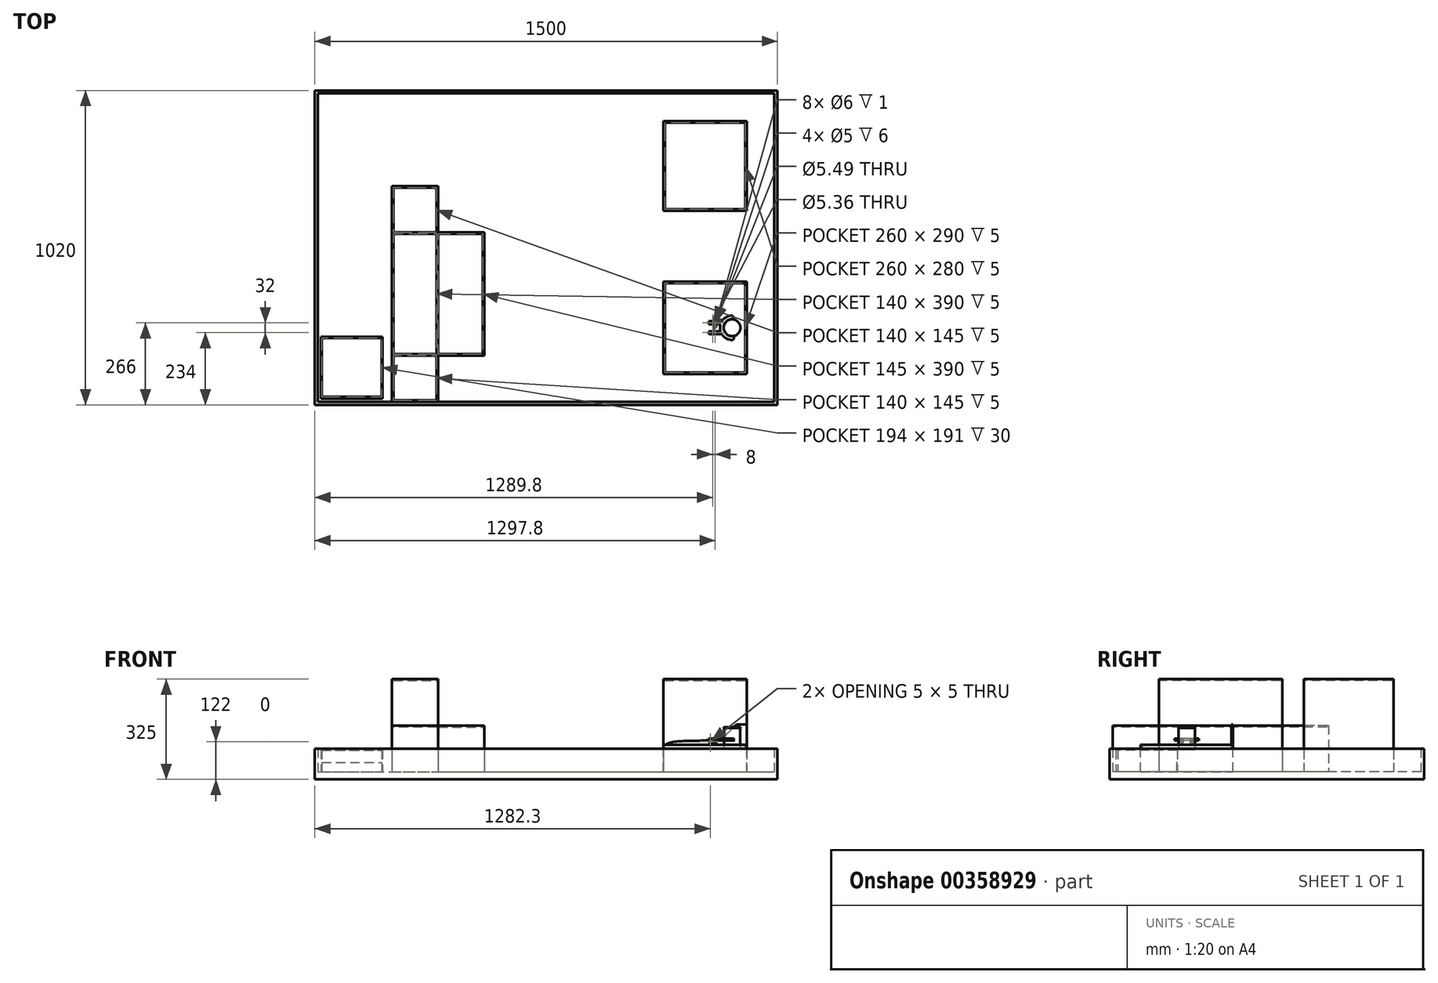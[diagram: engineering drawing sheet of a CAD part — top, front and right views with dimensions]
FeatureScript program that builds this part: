
annotation { "Feature Type Name" : "Feature", "Feature Type Description" : "" }
export const myFeature = defineFeature(function(context is Context, id is Id, definition is map)
    precondition{}
    {
        {
            var Q0;
            Q0=qCreatedBy(makeId("Top.planeOp"),FACE);
            var sketch = newSketch(context, id + "F0", { "sketchPlane" : qUnion([Q0])});
            skCircle(sketch, "E0", {"center": v(0, 0) * mm, "radius": 27.2 * mm});
            skSolve(sketch);
        }
        {
            var Q0;
            Q0=qSketchRegion(id+"F0",true);
            extrude(context, id + "F1", {"entities" : qUnion([Q0]), "depth" : 2.83 * mm});
        }
        {
            var Q0;
            Q0=makeQuery(id+"F1.opExtrude","CAP_FACE",FACE,{"disambiguationData":[OSD([sQuery(id+"F0.wireOp",EDGE,"E0")])],"isStart":false});
            var sketch = newSketch(context, id + "F2", { "sketchPlane" : qUnion([Q0])});
            skCircle(sketch, "E1", {"center": v(0, 0) * mm, "radius": 26.4 * mm});
            skSolve(sketch);
        }
        {
            var Q0;
            Q0=qSketchRegion(id+"F2",true);
            extrude(context, id + "F3", {"entities" : qUnion([Q0]), "operationType" : NewBodyOperationType.ADD, "depth" : 67.36 * mm});
        }
        {
            var Q0;
            Q0=makeQuery(id+"F3.opExtrude","CAP_FACE",FACE,{"disambiguationData":[OSD([sQuery(id+"F2.wireOp",EDGE,"E1")])],"isStart":false});
            var sketch = newSketch(context, id + "F4", { "sketchPlane" : qUnion([Q0])});
            skCircle(sketch, "E2", {"center": v(0, 0) * mm, "radius": 27.2 * mm});
            skSolve(sketch);
        }
        {
            var Q0;
            Q0=qSketchRegion(id+"F4",true);
            extrude(context, id + "F5", {"entities" : qUnion([Q0]), "operationType" : NewBodyOperationType.ADD, "depth" : 2.83 * mm});
        }
        {
            var Q0;
            Q0=makeQuery(id+"F5.opExtrude","CAP_FACE",FACE,{"disambiguationData":[OSD([sQuery(id+"F4.wireOp",EDGE,"E2")])],"isStart":false});
            var sketch = newSketch(context, id + "F6", { "sketchPlane" : qUnion([Q0])});
            skSolve(sketch);
        }
        {
            var Q0;
            Q0=qCreatedBy(makeId("Top.planeOp"),FACE);
            cPlane(context, id + "F7", {"entities" : qUnion([Q0]), "cplaneType" : CPlaneType.OFFSET, "offset" : 25 * mm, "width" : 150 * mm, "height" : 150 * mm});
        }
        {
            var Q0;
            Q0=makeQuery(id+"F6.imprint","IMPRINT",FACE,{"disambiguationData":[TD([[makeQuery(id+"F6.imprint","IMPRINT",EDGE,{"derivedFrom":makeQuery(id+"F5.opExtrude","CAP_EDGE",EDGE,{"disambiguationData":[OSD([sQuery(id+"F4.wireOp",EDGE,"E2")])],"isStart":false})}),1.0]])]});
            var sketch = newSketch(context, id + "F8", { "sketchPlane" : qUnion([Q0])});
            skSolve(sketch);
        }
        {
            var Q0;
            Q0=qCreatedBy(makeId("Top.planeOp"),FACE);
            var sketch = newSketch(context, id + "F9", { "sketchPlane" : qUnion([Q0])});
            skLineSegment(sketch, "E3.bottom", {"start": v(-222.8, -150) * mm, "end": v(47.2, -150) * mm});
            skLineSegment(sketch, "E3.top", {"start": v(-222.8, 150) * mm, "end": v(47.2, 150) * mm});
            skLineSegment(sketch, "E3.left", {"start": v(-222.8, -150) * mm, "end": v(-222.8, 150) * mm});
            skLineSegment(sketch, "E3.right", {"start": v(47.2, -150) * mm, "end": v(47.2, 150) * mm});
            skSolve(sketch);
        }
        {
            var Q0;
            Q0=qSketchRegion(id+"F9",true);
            extrude(context, id + "F10", {"entities" : qUnion([Q0]), "oppositeDirection" : true, "depth" : 72 * mm});
        }
        {
            var Q0;
            Q0=makeQuery(id+"F10.opExtrude","CAP_FACE",FACE,{"disambiguationData":[OSD([sQuery(id+"F9.wireOp",EDGE,"E3.bottom"),sQuery(id+"F9.wireOp",EDGE,"E3.top"),sQuery(id+"F9.wireOp",EDGE,"E3.left"),sQuery(id+"F9.wireOp",EDGE,"E3.right")])],"isStart":true});
            var sketch = newSketch(context, id + "F11", { "sketchPlane" : qUnion([Q0])});
            skLineSegment(sketch, "E4.bottom", {"start": v(-222.8, -150) * mm, "end": v(47.2, -150) * mm});
            skLineSegment(sketch, "E4.top", {"start": v(-222.8, -145) * mm, "end": v(42.2, -145) * mm});
            skLineSegment(sketch, "E4.left", {"start": v(-222.8, -150) * mm, "end": v(-222.8, -145) * mm});
            skLineSegment(sketch, "E5.bottom", {"start": v(47.2, 150) * mm, "end": v(42.2, 150) * mm});
            skLineSegment(sketch, "E5.left", {"start": v(47.2, 150) * mm, "end": v(47.2, -150) * mm});
            skLineSegment(sketch, "E5.right", {"start": v(42.2, 150) * mm, "end": v(42.2, -145) * mm});
            skSolve(sketch);
        }
        {
            var Q0;
            Q0=qSketchRegion(id+"F11",true);
            extrude(context, id + "F12", {"entities" : qUnion([Q0]), "operationType" : NewBodyOperationType.ADD, "depth" : 15 * mm});
        }
        {
            var Q0;
            Q0=makeQuery(id+"F12.boolean.opBoolean","MERGE",FACE,{"derivedFrom":[makeQuery(id+"F10.opExtrude","SWEPT_FACE",FACE,{"disambiguationData":[OSD([sQuery(id+"F9.wireOp",EDGE,"E3.top")])]}),makeQuery(id+"F12.opExtrude","SWEPT_FACE",FACE,{"disambiguationData":[OSD([sQuery(id+"F11.wireOp",EDGE,"E5.bottom")])]})]});
            var sketch = newSketch(context, id + "F13", { "sketchPlane" : qUnion([Q0])});
            skLineSegment(sketch, "E6", {"start": v(-47.2, 81.36) * mm, "end": v(-21.31, 81.36) * mm});
            skFitSpline(sketch, "E7", {"points": [v(-21.31, 81.36) * mm, v(15.24, 52.01) * mm, v(114.14, 28.17) * mm, v(222.8, 0) * mm], "startDerivative": vector(181.02, 0.3) * mm, "endDerivative": vector(-1.73, -239.85) * mm});
            skLineSegment(sketch, "E8", {"start": v(-47.2, 81.36) * mm, "end": v(-47.2, -72) * mm});
            skLineSegment(sketch, "E9", {"start": v(-47.2, -72) * mm, "end": v(222.8, -72) * mm});
            skLineSegment(sketch, "E10", {"start": v(222.8, -72) * mm, "end": v(222.8, 0) * mm});
            skSolve(sketch);
        }
        {
            var Q0;
            Q0=qSketchRegion(id+"F13",true);
            extrude(context, id + "F14", {"entities" : qUnion([Q0]), "operationType" : NewBodyOperationType.ADD, "oppositeDirection" : true, "depth" : 5 * mm});
        }
        {
            var Q0;
            Q0=makeQuery(id+"F10.opExtrude","CAP_FACE",FACE,{"disambiguationData":[OSD([sQuery(id+"F9.wireOp",EDGE,"E3.bottom"),sQuery(id+"F9.wireOp",EDGE,"E3.top"),sQuery(id+"F9.wireOp",EDGE,"E3.left"),sQuery(id+"F9.wireOp",EDGE,"E3.right")])],"isStart":true});
            var sketch = newSketch(context, id + "F15", { "sketchPlane" : qUnion([Q0])});
            skLineSegment(sketch, "E11.bottom", {"start": v(-222.8, 145) * mm, "end": v(-217.8, 145) * mm});
            skLineSegment(sketch, "E11.top", {"start": v(-222.8, -145) * mm, "end": v(-217.8, -145) * mm});
            skLineSegment(sketch, "E11.left", {"start": v(-222.8, 145) * mm, "end": v(-222.8, -145) * mm});
            skLineSegment(sketch, "E11.right", {"start": v(-217.8, 145) * mm, "end": v(-217.8, -145) * mm});
            skSolve(sketch);
        }
        {
            var Q0;
            Q0=qSketchRegion(id+"F15",true);
            extrude(context, id + "F16", {"entities" : qUnion([Q0]), "operationType" : NewBodyOperationType.ADD, "depth" : 5 * mm});
        }
        {
            var Q0;
            Q0=makeQuery(id+"F10.opExtrude","CAP_FACE",FACE,{"disambiguationData":[OSD([sQuery(id+"F9.wireOp",EDGE,"E3.bottom"),sQuery(id+"F9.wireOp",EDGE,"E3.top"),sQuery(id+"F9.wireOp",EDGE,"E3.left"),sQuery(id+"F9.wireOp",EDGE,"E3.right")])],"isStart":false});
            var sketch = newSketch(context, id + "F17", { "sketchPlane" : qUnion([Q0])});
            skLineSegment(sketch, "E12.bottom", {"start": v(147.2, 250) * mm, "end": v(-1352.8, 250) * mm});
            skLineSegment(sketch, "E12.top", {"start": v(147.2, -770) * mm, "end": v(-1352.8, -770) * mm});
            skLineSegment(sketch, "E12.left", {"start": v(147.2, 250) * mm, "end": v(147.2, -770) * mm});
            skLineSegment(sketch, "E12.right", {"start": v(-1352.8, 250) * mm, "end": v(-1352.8, -770) * mm});
            skSolve(sketch);
        }
        {
            var Q0;
            Q0=qSketchRegion(id+"F17",true);
            extrude(context, id + "F18", {"entities" : qUnion([Q0]), "operationType" : NewBodyOperationType.ADD, "depth" : 25 * mm});
        }
        {
            var Q0;
            Q0=makeQuery(id+"F18.opExtrude","CAP_FACE",FACE,{"disambiguationData":[OSD([sQuery(id+"F17.wireOp",EDGE,"E12.bottom"),sQuery(id+"F17.wireOp",EDGE,"E12.top"),sQuery(id+"F17.wireOp",EDGE,"E12.left"),sQuery(id+"F17.wireOp",EDGE,"E12.right")])],"isStart":true});
            var sketch = newSketch(context, id + "F19", { "sketchPlane" : qUnion([Q0])});
            skLineSegment(sketch, "E13.bottom", {"start": v(-222.8, 670) * mm, "end": v(47.2, 670) * mm});
            skLineSegment(sketch, "E13.top", {"start": v(-222.8, 380) * mm, "end": v(47.2, 380) * mm});
            skLineSegment(sketch, "E13.left", {"start": v(-222.8, 670) * mm, "end": v(-222.8, 380) * mm});
            skLineSegment(sketch, "E13.right", {"start": v(47.2, 670) * mm, "end": v(47.2, 380) * mm});
            skSolve(sketch);
        }
        {
            var Q0;
            Q0=qSketchRegion(id+"F19",true);
            extrude(context, id + "F20", {"entities" : qUnion([Q0]), "operationType" : NewBodyOperationType.ADD, "depth" : 300 * mm});
        }
        {
            var Q0;
            Q0=makeQuery(id+"F20.opExtrude","CAP_FACE",FACE,{"disambiguationData":[OSD([sQuery(id+"F19.wireOp",EDGE,"E13.bottom"),sQuery(id+"F19.wireOp",EDGE,"E13.top"),sQuery(id+"F19.wireOp",EDGE,"E13.left"),sQuery(id+"F19.wireOp",EDGE,"E13.right")])],"isStart":false});
            var sketch = newSketch(context, id + "F21", { "sketchPlane" : qUnion([Q0])});
            skLineSegment(sketch, "E14.bottom", {"start": v(-217.8, 665) * mm, "end": v(42.2, 665) * mm});
            skLineSegment(sketch, "E14.top", {"start": v(-217.8, 385) * mm, "end": v(42.2, 385) * mm});
            skLineSegment(sketch, "E14.left", {"start": v(-217.8, 665) * mm, "end": v(-217.8, 385) * mm});
            skLineSegment(sketch, "E14.right", {"start": v(42.2, 665) * mm, "end": v(42.2, 385) * mm});
            skSolve(sketch);
        }
        {
            var Q0;
            Q0=qSketchRegion(id+"F21",true);
            extrude(context, id + "F22", {"entities" : qUnion([Q0]), "operationType" : NewBodyOperationType.REMOVE, "oppositeDirection" : true, "depth" : 5 * mm});
        }
        {
            var Q0;
            Q0=makeQuery(id+"F18.opExtrude","CAP_FACE",FACE,{"disambiguationData":[OSD([sQuery(id+"F17.wireOp",EDGE,"E12.bottom"),sQuery(id+"F17.wireOp",EDGE,"E12.top"),sQuery(id+"F17.wireOp",EDGE,"E12.left"),sQuery(id+"F17.wireOp",EDGE,"E12.right")])],"isStart":true});
            var sketch = newSketch(context, id + "F23", { "sketchPlane" : qUnion([Q0])});
            skLineSegment(sketch, "E15.bottom", {"start": v(-1352.8, 770) * mm, "end": v(147.2, 770) * mm});
            skLineSegment(sketch, "E15.top", {"start": v(-1352.8, -250) * mm, "end": v(147.2, -250) * mm});
            skLineSegment(sketch, "E15.left", {"start": v(-1352.8, 770) * mm, "end": v(-1352.8, -250) * mm});
            skLineSegment(sketch, "E15.right", {"start": v(147.2, 770) * mm, "end": v(147.2, -250) * mm});
            skLineSegment(sketch, "E16.bottom", {"start": v(-1342.8, 760) * mm, "end": v(137.2, 760) * mm});
            skLineSegment(sketch, "E16.top", {"start": v(-1342.8, -240) * mm, "end": v(137.2, -240) * mm});
            skLineSegment(sketch, "E16.left", {"start": v(-1342.8, 760) * mm, "end": v(-1342.8, -240) * mm});
            skLineSegment(sketch, "E16.right", {"start": v(137.2, 760) * mm, "end": v(137.2, -240) * mm});
            skSolve(sketch);
        }
        {
            var Q0;
            Q0=qSketchRegion(id+"F23",true);
            extrude(context, id + "F24", {"entities" : qUnion([Q0]), "operationType" : NewBodyOperationType.ADD, "depth" : 75 * mm});
        }
        {
            var Q0;
            Q0=makeQuery(id+"F18.opExtrude","CAP_FACE",FACE,{"disambiguationData":[OSD([sQuery(id+"F17.wireOp",EDGE,"E12.bottom"),sQuery(id+"F17.wireOp",EDGE,"E12.top"),sQuery(id+"F17.wireOp",EDGE,"E12.left"),sQuery(id+"F17.wireOp",EDGE,"E12.right")])],"isStart":true});
            var sketch = newSketch(context, id + "F25", { "sketchPlane" : qUnion([Q0])});
            skLineSegment(sketch, "E17.bottom", {"start": v(-1102.8, 460) * mm, "end": v(-952.8, 460) * mm});
            skLineSegment(sketch, "E17.top", {"start": v(-1102.8, -240) * mm, "end": v(-952.8, -240) * mm});
            skLineSegment(sketch, "E17.left", {"start": v(-1102.8, 460) * mm, "end": v(-1102.8, -240) * mm});
            skLineSegment(sketch, "E17.right", {"start": v(-952.8, 460) * mm, "end": v(-952.8, 310) * mm});
            skLineSegment(sketch, "E18.bottom", {"start": v(-952.8, 310) * mm, "end": v(-802.8, 310) * mm});
            skLineSegment(sketch, "E18.top", {"start": v(-952.8, -90) * mm, "end": v(-802.8, -90) * mm});
            skLineSegment(sketch, "E18.right", {"start": v(-802.8, 310) * mm, "end": v(-802.8, -90) * mm});
            skLineSegment(sketch, "E19.trimOffspring", {"start": v(-952.8, -90) * mm, "end": v(-952.8, -240) * mm});
            skSolve(sketch);
        }
        {
            var Q0;
            Q0=qSketchRegion(id+"F25",true);
            extrude(context, id + "F26", {"entities" : qUnion([Q0]), "operationType" : NewBodyOperationType.ADD, "depth" : 150 * mm});
        }
        {
            var Q0;
            Q0=makeQuery(id+"F26.opExtrude","CAP_FACE",FACE,{"disambiguationData":[OSD([sQuery(id+"F25.wireOp",EDGE,"E17.bottom"),sQuery(id+"F25.wireOp",EDGE,"E17.top"),sQuery(id+"F25.wireOp",EDGE,"E17.left"),sQuery(id+"F25.wireOp",EDGE,"E17.right"),sQuery(id+"F25.wireOp",EDGE,"E18.bottom"),sQuery(id+"F25.wireOp",EDGE,"E18.top"),sQuery(id+"F25.wireOp",EDGE,"E18.right"),sQuery(id+"F25.wireOp",EDGE,"E19.trimOffspring")])],"isStart":false});
            var sketch = newSketch(context, id + "F27", { "sketchPlane" : qUnion([Q0])});
            skLineSegment(sketch, "E20.bottom", {"start": v(-952.8, 310) * mm, "end": v(-1102.8, 310) * mm});
            skLineSegment(sketch, "E20.top", {"start": v(-952.8, -90) * mm, "end": v(-1102.8, -90) * mm});
            skLineSegment(sketch, "E20.left", {"start": v(-952.8, 310) * mm, "end": v(-952.8, -90) * mm});
            skLineSegment(sketch, "E20.right", {"start": v(-1102.8, 310) * mm, "end": v(-1102.8, -90) * mm});
            skSolve(sketch);
        }
        {
            var Q0;
            Q0=qSketchRegion(id+"F27",true);
            extrude(context, id + "F28", {"entities" : qUnion([Q0]), "operationType" : NewBodyOperationType.ADD, "depth" : 150 * mm});
        }
        {
            var Q0;
            Q0=makeQuery(id+"F28.opExtrude","CAP_FACE",FACE,{"disambiguationData":[OSD([sQuery(id+"F27.wireOp",EDGE,"E20.bottom"),sQuery(id+"F27.wireOp",EDGE,"E20.top"),sQuery(id+"F27.wireOp",EDGE,"E20.left"),sQuery(id+"F27.wireOp",EDGE,"E20.right")])],"isStart":false});
            var sketch = newSketch(context, id + "F29", { "sketchPlane" : qUnion([Q0])});
            skLineSegment(sketch, "E21.bottom", {"start": v(-1097.8, 305) * mm, "end": v(-957.8, 305) * mm});
            skLineSegment(sketch, "E21.top", {"start": v(-1097.8, -85) * mm, "end": v(-957.8, -85) * mm});
            skLineSegment(sketch, "E21.left", {"start": v(-1097.8, 305) * mm, "end": v(-1097.8, -85) * mm});
            skLineSegment(sketch, "E21.right", {"start": v(-957.8, 305) * mm, "end": v(-957.8, -85) * mm});
            skSolve(sketch);
        }
        {
            var Q0;
            Q0=qSketchRegion(id+"F29",true);
            extrude(context, id + "F30", {"entities" : qUnion([Q0]), "operationType" : NewBodyOperationType.REMOVE, "oppositeDirection" : true, "depth" : 5 * mm});
        }
        {
            var Q0;
            {var subQ0=sQuery(id+"F25.wireOp",EDGE,"E17.left");var subQ1=sQuery(id+"F25.wireOp",EDGE,"E18.bottom");var subQ2=sQuery(id+"F25.wireOp",EDGE,"E17.right");var subQ3=sQuery(id+"F25.wireOp",EDGE,"E17.bottom");var subQ4=makeQuery(id+"F26.opExtrude","CAP_FACE",FACE,{"disambiguationData":[OSD([subQ3,sQuery(id+"F25.wireOp",EDGE,"E17.top"),subQ0,subQ2,subQ1,sQuery(id+"F25.wireOp",EDGE,"E18.top"),sQuery(id+"F25.wireOp",EDGE,"E18.right"),sQuery(id+"F25.wireOp",EDGE,"E19.trimOffspring")])],"isStart":false});Q0=makeQuery(id+"F28.boolean.opBoolean","SPLIT",FACE,{"disambiguationData":[TD([makeQuery(id+"F26.opExtrude","SWEPT_FACE",FACE,{"disambiguationData":[OSD([subQ3])]})])],"derivedFrom":subQ4});}
            var sketch = newSketch(context, id + "F31", { "sketchPlane" : qUnion([Q0])});
            skLineSegment(sketch, "E22.bottom", {"start": v(-1097.8, 455) * mm, "end": v(-957.8, 455) * mm});
            skLineSegment(sketch, "E22.top", {"start": v(-1097.8, 310) * mm, "end": v(-957.8, 310) * mm});
            skLineSegment(sketch, "E22.left", {"start": v(-1097.8, 455) * mm, "end": v(-1097.8, 310) * mm});
            skLineSegment(sketch, "E22.right", {"start": v(-957.8, 455) * mm, "end": v(-957.8, 310) * mm});
            skLineSegment(sketch, "E23.bottom", {"start": v(-952.8, 305) * mm, "end": v(-807.8, 305) * mm});
            skLineSegment(sketch, "E23.top", {"start": v(-952.8, -85) * mm, "end": v(-807.8, -85) * mm});
            skLineSegment(sketch, "E23.left", {"start": v(-952.8, 305) * mm, "end": v(-952.8, -85) * mm});
            skLineSegment(sketch, "E23.right", {"start": v(-807.8, 305) * mm, "end": v(-807.8, -85) * mm});
            skLineSegment(sketch, "E24.bottom", {"start": v(-1097.8, -90) * mm, "end": v(-957.8, -90) * mm});
            skLineSegment(sketch, "E24.top", {"start": v(-1097.8, -235) * mm, "end": v(-957.8, -235) * mm});
            skLineSegment(sketch, "E24.left", {"start": v(-1097.8, -90) * mm, "end": v(-1097.8, -235) * mm});
            skLineSegment(sketch, "E24.right", {"start": v(-957.8, -90) * mm, "end": v(-957.8, -235) * mm});
            skSolve(sketch);
        }
        {
            var Q0;
            Q0=qSketchRegion(id+"F31",true);
            extrude(context, id + "F32", {"entities" : qUnion([Q0]), "operationType" : NewBodyOperationType.REMOVE, "oppositeDirection" : true, "depth" : 5 * mm});
        }
        {
            var Q0;
            Q0=qCreatedBy(id+"F7.planeOp",FACE);
            var sketch = newSketch(context, id + "F33", { "sketchPlane" : qUnion([Q0])});
            skLineSegment(sketch, "E25", {"start": v(0, 0) * mm, "end": v(-90, 0) * mm, "construction": true});
            skLineSegment(sketch, "E26.bottom", {"start": v(-74.5, -12) * mm, "end": v(-55, -12) * mm});
            skLineSegment(sketch, "E26.top", {"start": v(-74.5, -20) * mm, "end": v(-55, -20) * mm});
            skLineSegment(sketch, "E26.left", {"start": v(-74.5, -12) * mm, "end": v(-74.5, -13) * mm});
            skPoint(sketch, "E27.visualSharp", {"position": v(-51, -12) * mm});
            skPoint(sketch, "E28.visualSharp", {"position": v(-51, -20) * mm});
            skCircle(sketch, "E29", {"center": v(-55, -16) * mm, "radius": 3 * mm});
            skLineSegment(sketch, "E30", {"start": v(-59, -3.98) * mm, "end": v(-59, -18.08) * mm, "construction": true});
            skCircle(sketch, "E31.MirrorC", {"center": v(-63, -16) * mm, "radius": 3 * mm});
            skLineSegment(sketch, "E32.bottom", {"start": v(-74.5, -13) * mm, "end": v(-65.65, -13) * mm});
            skLineSegment(sketch, "E32.top", {"start": v(-74.5, -19) * mm, "end": v(-65.65, -19) * mm});
            skArc(sketch, "E33", {"start": v(-65.65, -13) * mm, "mid": v(-67, -16) * mm, "end": v(-65.65, -19) * mm});
            skLineSegment(sketch, "E34.trimOffspring", {"start": v(-74.5, -19) * mm, "end": v(-74.5, -20) * mm});
            skArc(sketch, "E35.trimOffspring", {"start": v(-55, -20) * mm, "mid": v(-51, -16) * mm, "end": v(-55, -12) * mm});
            skLineSegment(sketch, "E36.MirrorCS", {"start": v(-74.5, 12) * mm, "end": v(-74.5, 13) * mm});
            skLineSegment(sketch, "E37.MirrorCS", {"start": v(-74.5, 19) * mm, "end": v(-74.5, 20) * mm});
            skPoint(sketch, "E38.MirrorP", {"position": v(-51, 12) * mm});
            skLineSegment(sketch, "E39.MirrorCS", {"start": v(-74.5, 12) * mm, "end": v(-55, 12) * mm});
            skPoint(sketch, "E40.MirrorP", {"position": v(-51, 20) * mm});
            skArc(sketch, "E41.MirrorCS", {"start": v(-65.65, 13) * mm, "mid": v(-67, 16) * mm, "end": v(-65.65, 19) * mm});
            skArc(sketch, "E42.MirrorCS", {"start": v(-55, 20) * mm, "mid": v(-51, 16) * mm, "end": v(-55, 12) * mm});
            skLineSegment(sketch, "E43.MirrorCS", {"start": v(-74.5, 20) * mm, "end": v(-55, 20) * mm});
            skCircle(sketch, "E44.MirrorC", {"center": v(-55, 16) * mm, "radius": 3 * mm});
            skCircle(sketch, "E45.MirrorC", {"center": v(-63, 16) * mm, "radius": 3 * mm});
            skLineSegment(sketch, "E46.MirrorCS", {"start": v(-74.5, 19) * mm, "end": v(-65.65, 19) * mm});
            skLineSegment(sketch, "E47.MirrorCS", {"start": v(-74.5, 13) * mm, "end": v(-65.65, 13) * mm});
            skSolve(sketch);
        }
        {
            var Q0;
            Q0=qSketchRegion(id+"F33",true);
            var Q1;
            Q1=qSketchRegion(id+"F36",true);
            extrude(context, id + "F34", {"entities" : qUnion([Q0, Q1]), "endBound" : BoundingType.SYMMETRIC, "depth" : 8 * mm});
        }
        {
            var Q0;
            Q0=makeQuery(id+"F34.opExtrude","CAP_EDGE",EDGE,{"disambiguationData":[OSD([sQuery(id+"F33.wireOp",EDGE,"E34.trimOffspring")])],"isStart":false});
            var Q1;
            Q1=makeQuery(id+"F34.opExtrude","CAP_EDGE",EDGE,{"disambiguationData":[OSD([sQuery(id+"F33.wireOp",EDGE,"E26.left")])],"isStart":false});
            var Q2;
            Q2=makeQuery(id+"F34.opExtrude","CAP_EDGE",EDGE,{"disambiguationData":[OSD([sQuery(id+"F33.wireOp",EDGE,"E34.trimOffspring")])],"isStart":true});
            var Q3;
            Q3=makeQuery(id+"F34.opExtrude","CAP_EDGE",EDGE,{"disambiguationData":[OSD([sQuery(id+"F33.wireOp",EDGE,"E26.left")])],"isStart":true});
            var Q4;
            Q4=makeQuery(id+"F34.opExtrude","CAP_EDGE",EDGE,{"disambiguationData":[OSD([sQuery(id+"F33.wireOp",EDGE,"E36.MirrorCS")])],"isStart":false});
            var Q5;
            Q5=makeQuery(id+"F34.opExtrude","CAP_EDGE",EDGE,{"disambiguationData":[OSD([sQuery(id+"F33.wireOp",EDGE,"E37.MirrorCS")])],"isStart":false});
            var Q6;
            Q6=makeQuery(id+"F34.opExtrude","CAP_EDGE",EDGE,{"disambiguationData":[OSD([sQuery(id+"F33.wireOp",EDGE,"E37.MirrorCS")])],"isStart":true});
            var Q7;
            Q7=makeQuery(id+"F34.opExtrude","CAP_EDGE",EDGE,{"disambiguationData":[OSD([sQuery(id+"F33.wireOp",EDGE,"E36.MirrorCS")])],"isStart":true});
            fillet(context, id + "F35", {"entities" : qUnion([Q0, Q1, Q2, Q3, Q4, Q5, Q6, Q7]), "radius" : 4 * mm, "tangentPropagation" : true, "allowEdgeOverflow" : false});
        }
        {
            var Q0;
            Q0=makeQuery(id+"F34.opExtrude","SWEPT_FACE",FACE,{"disambiguationData":[OSD([sQuery(id+"F33.wireOp",EDGE,"E26.top")])]});
            var sketch = newSketch(context, id + "F36", { "sketchPlane" : qUnion([Q0])});
            skCircle(sketch, "E48", {"center": v(-70.5, 25) * mm, "radius": 3 * mm});
            skSolve(sketch);
        }
        {
            var Q0;
            Q0=qSketchRegion(id+"F36",true);
            var Q1;
            Q1=makeQuery(id+"F34.opExtrude","SWEPT_FACE",FACE,{"disambiguationData":[OSD([sQuery(id+"F33.wireOp",EDGE,"E26.bottom")])]});
            extrude(context, id + "F37", {"entities" : qUnion([Q0]), "operationType" : NewBodyOperationType.ADD, "endBound" : BoundingType.UP_TO_SURFACE, "oppositeDirection" : true, "endBoundEntityFace" : qUnion([Q1]), "depth" : 25 * mm});
        }
        {
            var Q0;
            Q0=makeQuery(id+"F34.opExtrude","SWEPT_FACE",FACE,{"disambiguationData":[OSD([sQuery(id+"F33.wireOp",EDGE,"E43.MirrorCS")])]});
            var sketch = newSketch(context, id + "F38", { "sketchPlane" : qUnion([Q0])});
            skCircle(sketch, "E49", {"center": v(70.5, 25) * mm, "radius": 3 * mm});
            skSolve(sketch);
        }
        {
            var Q0;
            Q0=qSketchRegion(id+"F38",true);
            var Q1;
            Q1=makeQuery(id+"F34.opExtrude","SWEPT_FACE",FACE,{"disambiguationData":[OSD([sQuery(id+"F33.wireOp",EDGE,"E39.MirrorCS")])]});
            extrude(context, id + "F39", {"entities" : qUnion([Q0]), "operationType" : NewBodyOperationType.ADD, "endBound" : BoundingType.UP_TO_SURFACE, "oppositeDirection" : true, "endBoundEntityFace" : qUnion([Q1]), "depth" : 25 * mm});
        }
        {
            var Q0;
            Q0=qCreatedBy(id+"F7.planeOp",FACE);
            var sketch = newSketch(context, id + "F40", { "sketchPlane" : qUnion([Q0])});
            skCircle(sketch, "E50", {"center": v(-55, 16) * mm, "radius": 3 * mm});
            skCircle(sketch, "E51", {"center": v(-63, 16) * mm, "radius": 2.5 * mm});
            skCircle(sketch, "E52", {"center": v(-63, 16) * mm, "radius": 3 * mm});
            skCircle(sketch, "E53", {"center": v(-55, 16) * mm, "radius": 2.5 * mm});
            skSolve(sketch);
        }
        {
            var Q0;
            Q0=qSketchRegion(id+"F40",true);
            extrude(context, id + "F41", {"entities" : qUnion([Q0]), "operationType" : NewBodyOperationType.ADD, "endBound" : BoundingType.SYMMETRIC, "depth" : 6 * mm});
        }
        {
            var Q0;
            Q0=qCreatedBy(id+"F7.planeOp",FACE);
            var sketch = newSketch(context, id + "F42", { "sketchPlane" : qUnion([Q0])});
            skCircle(sketch, "E54", {"center": v(-63, -16) * mm, "radius": 2.5 * mm});
            skCircle(sketch, "E55", {"center": v(-63, -16) * mm, "radius": 3 * mm});
            skCircle(sketch, "E56", {"center": v(-55, -16) * mm, "radius": 2.5 * mm});
            skCircle(sketch, "E57", {"center": v(-55, -16) * mm, "radius": 3 * mm});
            skSolve(sketch);
        }
        {
            var Q0;
            Q0=qSketchRegion(id+"F42",true);
            extrude(context, id + "F43", {"entities" : qUnion([Q0]), "operationType" : NewBodyOperationType.ADD, "endBound" : BoundingType.SYMMETRIC, "depth" : 6 * mm});
        }
        {
            var Q0;
            Q0=makeQuery(id+"F34.opExtrude","SWEPT_FACE",FACE,{"disambiguationData":[OSD([sQuery(id+"F33.wireOp",EDGE,"E43.MirrorCS")])]});
            var sketch = newSketch(context, id + "F44", { "sketchPlane" : qUnion([Q0])});
            skArc(sketch, "E58", {"start": v(71.5, 27.3) * mm, "mid": v(70.5, 27.5) * mm, "end": v(69.5, 27.3) * mm});
            skLineSegment(sketch, "E59.bottom", {"start": v(68.2, 26) * mm, "end": v(69.5, 26) * mm});
            skLineSegment(sketch, "E59.top", {"start": v(68.2, 24) * mm, "end": v(69.5, 24) * mm});
            skLineSegment(sketch, "E60.left", {"start": v(71.5, 27.3) * mm, "end": v(71.5, 26) * mm});
            skLineSegment(sketch, "E60.right", {"start": v(69.5, 27.3) * mm, "end": v(69.5, 26) * mm});
            skPoint(sketch, "E61.orphan", {"position": v(69.5, 27.8) * mm});
            skPoint(sketch, "E62.orphan", {"position": v(71.5, 27.8) * mm});
            skArc(sketch, "E63.trimOffspring", {"start": v(68.2, 26) * mm, "mid": v(68, 25) * mm, "end": v(68.2, 24) * mm});
            skPoint(sketch, "E59.left.start.orphan", {"position": v(67.32, 26) * mm});
            skPoint(sketch, "E64.orphan", {"position": v(67.32, 24) * mm});
            skArc(sketch, "E65.trimOffspring", {"start": v(69.5, 22.7) * mm, "mid": v(70.5, 22.5) * mm, "end": v(71.5, 22.7) * mm});
            skLineSegment(sketch, "E66.trimOffspring", {"start": v(69.5, 24) * mm, "end": v(69.5, 22.7) * mm});
            skLineSegment(sketch, "E67.trimOffspring", {"start": v(71.5, 26) * mm, "end": v(72.8, 26) * mm});
            skLineSegment(sketch, "E68.trimOffspring", {"start": v(71.5, 24) * mm, "end": v(71.5, 22.7) * mm});
            skLineSegment(sketch, "E69.trimOffspring", {"start": v(71.5, 24) * mm, "end": v(72.8, 24) * mm});
            skPoint(sketch, "E60.top.end.orphan", {"position": v(69.5, 22.2) * mm});
            skPoint(sketch, "E70.orphan", {"position": v(71.5, 22.2) * mm});
            skPoint(sketch, "E59.right.end.orphan", {"position": v(73.68, 24) * mm});
            skPoint(sketch, "E71.orphan", {"position": v(73.68, 26) * mm});
            skArc(sketch, "E72.trimOffspring", {"start": v(72.8, 24) * mm, "mid": v(73, 25) * mm, "end": v(72.8, 26) * mm});
            skSolve(sketch);
        }
        {
            var Q0;
            Q0=qSketchRegion(id+"F44",true);
            extrude(context, id + "F45", {"entities" : qUnion([Q0]), "operationType" : NewBodyOperationType.REMOVE, "endBound" : BoundingType.THROUGH_ALL, "oppositeDirection" : true, "depth" : 25 * mm});
        }
        {
            var Q0;
            Q0=makeQuery(id+"F18.opExtrude","CAP_FACE",FACE,{"disambiguationData":[OSD([sQuery(id+"F17.wireOp",EDGE,"E12.bottom"),sQuery(id+"F17.wireOp",EDGE,"E12.top"),sQuery(id+"F17.wireOp",EDGE,"E12.left"),sQuery(id+"F17.wireOp",EDGE,"E12.right")])],"isStart":true});
            var sketch = newSketch(context, id + "F46", { "sketchPlane" : qUnion([Q0])});
            skLineSegment(sketch, "E73.bottom", {"start": v(-1332.8, -30) * mm, "end": v(-1132.8, -30) * mm});
            skLineSegment(sketch, "E73.top", {"start": v(-1332.8, -230) * mm, "end": v(-1132.8, -230) * mm});
            skLineSegment(sketch, "E73.left", {"start": v(-1332.8, -30) * mm, "end": v(-1332.8, -230) * mm});
            skLineSegment(sketch, "E73.right", {"start": v(-1132.8, -30) * mm, "end": v(-1132.8, -230) * mm});
            skLineSegment(sketch, "E74.bottom", {"start": v(-1329.8, -33) * mm, "end": v(-1135.8, -33) * mm});
            skLineSegment(sketch, "E74.top", {"start": v(-1329.8, -224) * mm, "end": v(-1135.8, -224) * mm});
            skLineSegment(sketch, "E74.left", {"start": v(-1329.8, -33) * mm, "end": v(-1329.8, -224) * mm});
            skLineSegment(sketch, "E74.right", {"start": v(-1135.8, -33) * mm, "end": v(-1135.8, -224) * mm});
            skSolve(sketch);
        }
        {
            var Q0;
            Q0=qSketchRegion(id+"F46",true);
            extrude(context, id + "F47", {"entities" : qUnion([Q0]), "operationType" : NewBodyOperationType.ADD, "depth" : 30 * mm});
        }
        {
            var Q0;
            Q0=makeQuery(id+"F47.opExtrude","CAP_FACE",FACE,{"disambiguationData":[OSD([sQuery(id+"F46.wireOp",EDGE,"E73.bottom"),sQuery(id+"F46.wireOp",EDGE,"E73.top"),sQuery(id+"F46.wireOp",EDGE,"E73.left"),sQuery(id+"F46.wireOp",EDGE,"E73.right"),sQuery(id+"F46.wireOp",EDGE,"E74.bottom"),sQuery(id+"F46.wireOp",EDGE,"E74.top"),sQuery(id+"F46.wireOp",EDGE,"E74.left"),sQuery(id+"F46.wireOp",EDGE,"E74.right")])],"isStart":false});
            var sketch = newSketch(context, id + "F48", { "sketchPlane" : qUnion([Q0])});
            skLineSegment(sketch, "E75.bottom", {"start": v(-1332.8, -30) * mm, "end": v(-1329.8, -30) * mm});
            skLineSegment(sketch, "E75.top", {"start": v(-1332.8, -230) * mm, "end": v(-1329.8, -230) * mm});
            skLineSegment(sketch, "E75.left", {"start": v(-1332.8, -30) * mm, "end": v(-1332.8, -230) * mm});
            skLineSegment(sketch, "E75.right", {"start": v(-1329.8, -30) * mm, "end": v(-1329.8, -224) * mm});
            skLineSegment(sketch, "E76.bottom", {"start": v(-1329.8, -230) * mm, "end": v(-1135.8, -230) * mm});
            skLineSegment(sketch, "E76.top", {"start": v(-1329.8, -224) * mm, "end": v(-1135.8, -224) * mm});
            skLineSegment(sketch, "E77.bottom", {"start": v(-1135.8, -230) * mm, "end": v(-1132.8, -230) * mm});
            skLineSegment(sketch, "E77.top", {"start": v(-1135.8, -30) * mm, "end": v(-1132.8, -30) * mm});
            skLineSegment(sketch, "E77.left", {"start": v(-1135.8, -224) * mm, "end": v(-1135.8, -30) * mm});
            skLineSegment(sketch, "E77.right", {"start": v(-1132.8, -230) * mm, "end": v(-1132.8, -30) * mm});
            skSolve(sketch);
        }
        {
            var Q0;
            Q0=qSketchRegion(id+"F48",true);
            extrude(context, id + "F49", {"entities" : qUnion([Q0]), "operationType" : NewBodyOperationType.ADD, "depth" : 40 * mm});
        }
        {
            var Q0;
            Q0=makeQuery(id+"F34.opExtrude","CAP_FACE",FACE,{"disambiguationData":[OSD([sQuery(id+"F33.wireOp",EDGE,"E36.MirrorCS"),sQuery(id+"F33.wireOp",EDGE,"E37.MirrorCS"),sQuery(id+"F33.wireOp",EDGE,"E39.MirrorCS"),sQuery(id+"F33.wireOp",EDGE,"E41.MirrorCS"),sQuery(id+"F33.wireOp",EDGE,"E42.MirrorCS"),sQuery(id+"F33.wireOp",EDGE,"E43.MirrorCS"),sQuery(id+"F33.wireOp",EDGE,"E44.MirrorC"),sQuery(id+"F33.wireOp",EDGE,"E45.MirrorC"),sQuery(id+"F33.wireOp",EDGE,"E46.MirrorCS"),sQuery(id+"F33.wireOp",EDGE,"E47.MirrorCS")])],"isStart":false});
            var sketch = newSketch(context, id + "F50", { "sketchPlane" : qUnion([Q0])});
            skLineSegment(sketch, "E78", {"start": v(-75.7, 21.02) * mm, "end": v(-75.7, 10.66) * mm});
            skLineSegment(sketch, "E79", {"start": v(-75.7, 10.66) * mm, "end": v(-36.68, 10.66) * mm});
            skLineSegment(sketch, "E80", {"start": v(-36.68, -11.44) * mm, "end": v(-75.3, -11.44) * mm});
            skLineSegment(sketch, "E81", {"start": v(-75.3, -11.44) * mm, "end": v(-75.3, -20.78) * mm});
            skArc(sketch, "E82", {"start": v(-0.27, 27.83) * mm, "mid": v(-27.17, -0.1) * mm, "end": v(0.44, -27.34) * mm});
            skArc(sketch, "E83.0", {"start": v(-0.57, 39.82) * mm, "mid": v(-19.31, 34.57) * mm, "end": v(-33.28, 21.02) * mm});
            skLineSegment(sketch, "E84", {"start": v(-75.7, 21.02) * mm, "end": v(-33.28, 21.02) * mm});
            skArc(sketch, "E85", {"start": v(-0.27, 27.83) * mm, "mid": v(3.98, 33.93) * mm, "end": v(-0.57, 39.82) * mm});
            skArc(sketch, "E86", {"start": v(0.45, -39.34) * mm, "mid": v(6.06, -33.34) * mm, "end": v(0.44, -27.34) * mm});
            skArc(sketch, "E87.trimOffspring", {"start": v(-37.78, 10.66) * mm, "mid": v(-39.16, -0.41) * mm, "end": v(-37.4, -11.44) * mm});
            skArc(sketch, "E88.trimOffspring", {"start": v(-33.13, -20.78) * mm, "mid": v(-18.74, -34.4) * mm, "end": v(0.45, -39.34) * mm});
            skLineSegment(sketch, "E89", {"start": v(-75.3, -20.78) * mm, "end": v(-33.13, -20.78) * mm});
            skCircle(sketch, "E90", {"center": v(-63, -16) * mm, "radius": 2.64 * mm});
            skCircle(sketch, "E91", {"center": v(-55.05, -16) * mm, "radius": 2.52 * mm});
            skCircle(sketch, "E92", {"center": v(-63, 16) * mm, "radius": 2.68 * mm});
            skCircle(sketch, "E93", {"center": v(-55, 16) * mm, "radius": 2.74 * mm});
            skSolve(sketch);
        }
        {
            var Q0;
            Q0 = qSketchRegion(id + "F50", true);
            extrude(context, id + "F51", {"entities" : qUnion([Q0]), "depth" : 6 * mm});
        }
    });
